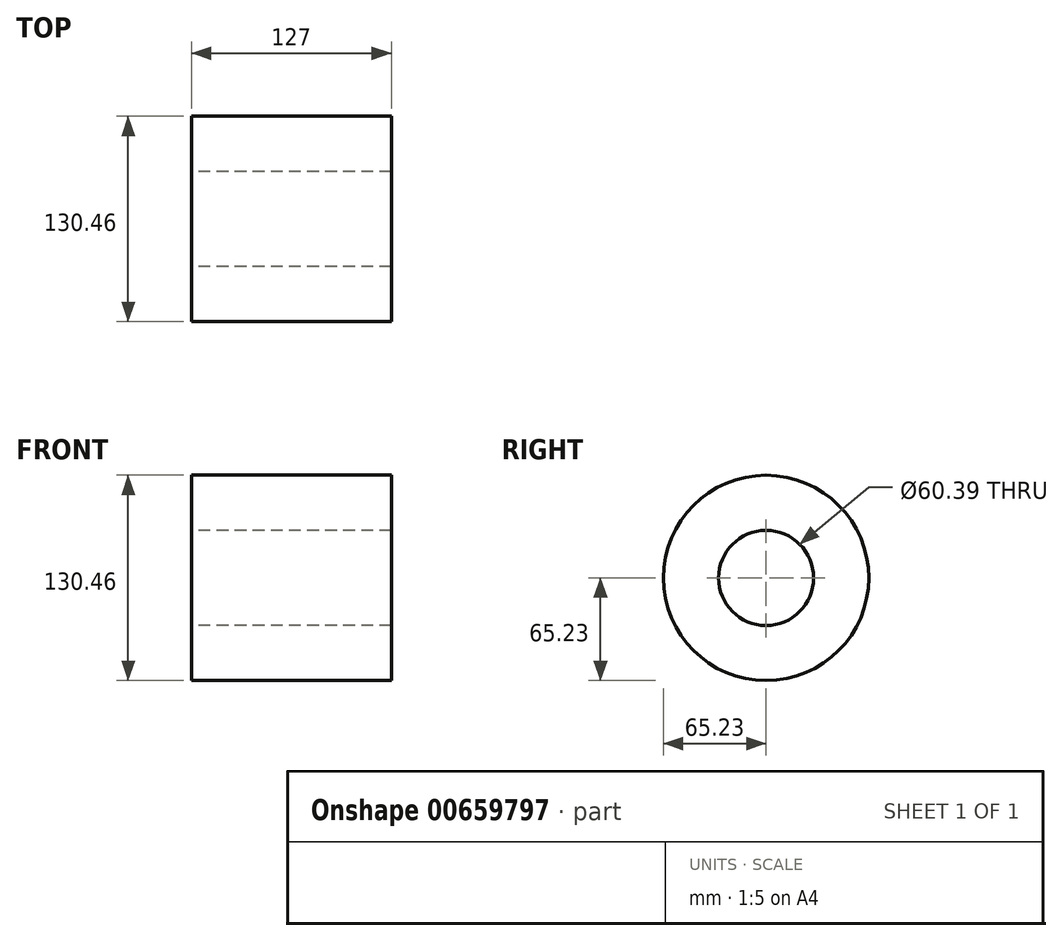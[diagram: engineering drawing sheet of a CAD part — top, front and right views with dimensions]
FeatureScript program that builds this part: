
annotation { "Feature Type Name" : "Feature", "Feature Type Description" : "" }
export const myFeature = defineFeature(function(context is Context, id is Id, definition is map)
    precondition{}
    {
        {
            var Q0;
            Q0=qCreatedBy(makeId("Right.planeOp"),FACE);
            var sketch = newSketch(context, id + "F0", { "sketchPlane" : qUnion([Q0])});
            skCircle(sketch, "E0", {"center": v(0, 0) * mm, "radius": 65.23 * mm});
            skCircle(sketch, "E1", {"center": v(0, 0) * mm, "radius": 30.2 * mm});
            skSolve(sketch);
        }
        {
            var Q0;
            Q0=makeQuery(id+"F0.imprint","IMPRINT",FACE,{"disambiguationData":[TD([[makeQuery(id+"F0.imprint","IMPRINT",EDGE,{"derivedFrom":sQuery(id+"F0.wireOp",EDGE,"E0")}),1.0]])]});
            extrude(context, id + "F1", {"entities" : qUnion([Q0]), "depth" : 127 * mm, "offsetDistance" : 25.4 * mm});
        }
    });
